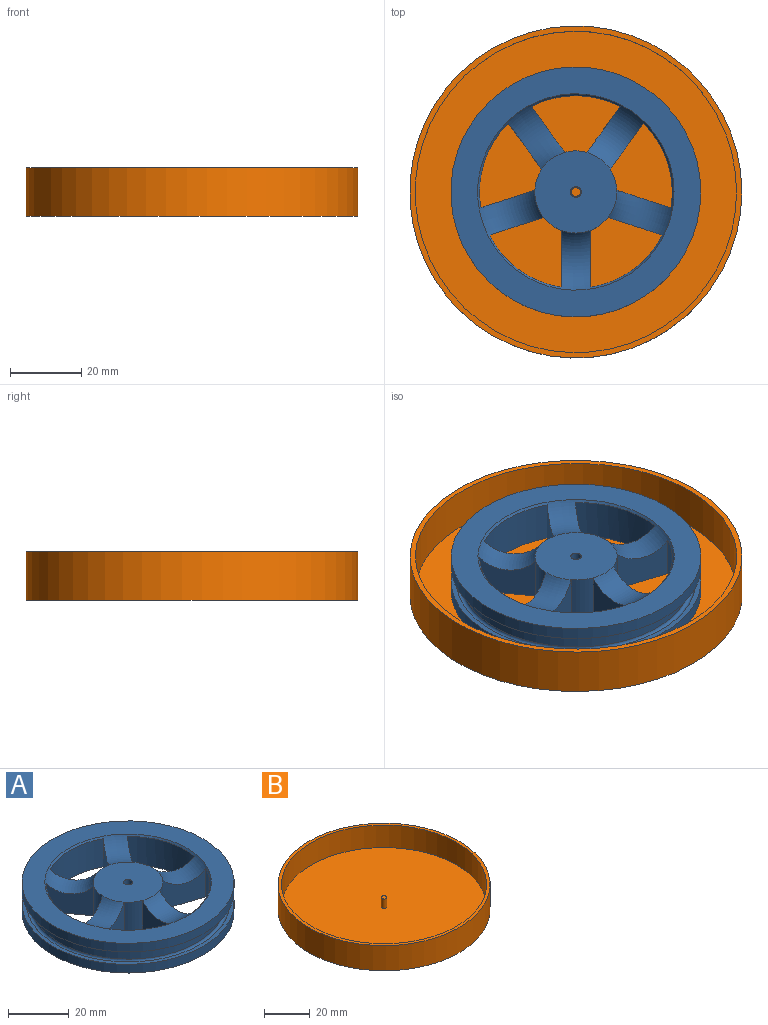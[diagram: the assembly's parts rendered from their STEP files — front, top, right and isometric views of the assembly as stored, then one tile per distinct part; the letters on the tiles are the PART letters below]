
ASSEMBLY  parts=2 mates=1
PART A: 33 faces, bbox 72.8x72.8x18 mm
  f0: plane 23x23mm, normal (0,0,1), area 408.4mm2, adj f2,f5,f8,f11,f14,f20,f24,f25
  f1: plane 15.15x12.01mm, normal (0.31,0.95,0), area 145.4mm2, adj f2,f22,f23,f24,f25
  f2: cylinder r=11.5mm len=12mm, axis (0,0,-1), area 75.4mm2, adj f0,f1,f3,f23
  f3: plane 12.88x12mm, normal (0.81,-0.59,0), area 145.4mm2, adj f2,f22,f23,f24
  f4: plane 15.14x12mm, normal (0.31,-0.95,0), area 145.4mm2, adj f5,f16,f23,f24
  f5: cylinder r=11.5mm len=12mm, axis (0,0,-1), area 75.4mm2, adj f0,f4,f6,f23
  f6: plane 15.93x12.01mm, normal (-1,0,0), area 145.4mm2, adj f5,f16,f23,f24
  f7: plane 12.88x12mm, normal (-0.81,-0.59,0), area 145.4mm2, adj f8,f17,f23,f24
  f8: cylinder r=11.5mm len=12mm, axis (0,0,-1), area 75.4mm2, adj f0,f7,f9,f23
  f9: plane 15.14x12mm, normal (-0.31,0.95,0), area 145.4mm2, adj f8,f17,f23,f24
  f10: plane 12.88x12mm, normal (-0.81,0.59,0), area 145.4mm2, adj f11,f18,f23,f24
  f11: cylinder r=11.5mm len=12mm, axis (0,0,-1), area 75.4mm2, adj f0,f10,f12,f23
  f12: plane 12.88x12mm, normal (0.81,0.59,0), area 145.4mm2, adj f11,f18,f23,f24
  f13: plane 15.93x12.01mm, normal (1,0,0), area 145.4mm2, adj f14,f21,f23,f24
  f14: cylinder r=11.5mm len=12mm, axis (0,0,-1), area 75.4mm2, adj f0,f13,f15,f23
  f15: plane 15.14x12mm, normal (-0.31,-0.95,0), area 145.4mm2, adj f14,f21,f23,f24
  f16: cylinder r=27mm len=20.16mm, axis (0,0,-1), area 294.9mm2, adj f4,f6,f23,f24
  f17: cylinder r=27mm len=23.7mm, axis (0,0,-1), area 294.9mm2, adj f7,f9,f23,f24
  f18: cylinder r=27mm len=24.92mm, axis (0,0,-1), area 294.9mm2, adj f10,f12,f23,f24
  f19: cylinder r=35mm len=70mm, axis (0,0,-1), area 772.8mm2, adj f23,f26
  f20: cylinder r=1.5mm len=12mm, axis (0,0,-1), area 113.1mm2, adj f0,f23
  f21: cylinder r=27mm len=20.16mm, axis (0,0,-1), area 294.9mm2, adj f13,f15,f23,f24
  f22: cylinder r=27mm len=23.7mm, axis (0,0,-1), area 294.9mm2, adj f1,f3,f23,f24
  f23: plane 70x70mm, normal (0,0,-1), area 2592.1mm2, adj f1,f2,f3,f4,f5,f6,f7,f8
  f24: torus R=19.5mm, axis (0,0,1), area 851.8mm2, adj f0,f1,f3,f4,f6,f7,f9,f10
  f25: torus R=19.5mm, axis (0,0,1), area 0.5mm2, adj f0,f1,f24
  f26: plane 70x70mm, normal (0,0,1), area 301.7mm2, adj f19,f27
  f27: torus R=32.8mm, axis (0,0,1), area 518mm2, adj f26,f28
  f28: cylinder r=32mm len=64mm, axis (0,0,1), area 1005.3mm2, adj f27,f29
  f29: torus R=32.8mm, axis (0,0,1), area 518mm2, adj f28,f30
  f30: plane 70x70mm, normal (0,0,-1), area 301.7mm2, adj f29,f32
  f31: plane 70x70mm, normal (0,0,1), area 1472.6mm2, adj f24,f32
  f32: cylinder r=35mm len=70mm, axis (0,0,-1), area 766.6mm2, adj f30,f31
PART B: 7 faces, bbox 93x93x13.5 mm
  f0: cylinder r=46.5mm len=93mm, axis (0,0,1), area 3944.3mm2, adj f1,f3
  f1: plane 93x93mm, normal (0,0,-1), area 6792.9mm2, adj f0
  f2: cylinder r=45mm len=90mm, axis (0,0,-1), area 3392.9mm2, adj f3,f4
  f3: plane 93x93mm, normal (0,0,1), area 431.2mm2, adj f0,f2
  f4: plane 90x90mm, normal (0,0,1), area 6356.8mm2, adj f2,f5
  f5: cylinder r=1.25mm len=5mm, axis (0,0,-1), area 39.3mm2, adj f4,f6
  f6: plane 2.5x2.5mm, normal (0,0,1), area 4.9mm2, adj f5
PLACE A t=(6.19,-158.88,-50.91)mm
PLACE B t=(6.19,-158.88,-50.91)mm
MATE fastened A.f2 <-> B.f2  axis (0,0,-1) through (6.19,-158.88,-50.91)mm
